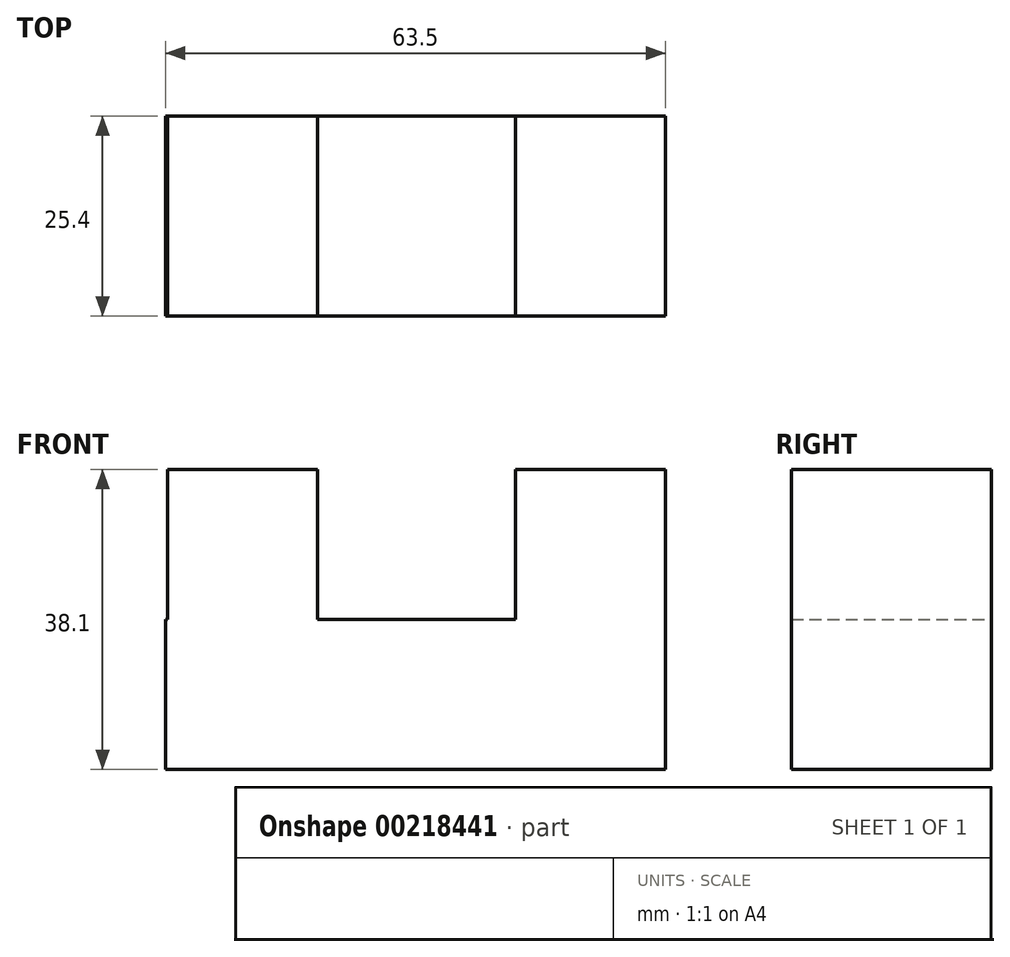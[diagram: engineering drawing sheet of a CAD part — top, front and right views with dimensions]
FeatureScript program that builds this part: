
annotation { "Feature Type Name" : "Feature", "Feature Type Description" : "" }
export const myFeature = defineFeature(function(context is Context, id is Id, definition is map)
    precondition{}
    {
        {
            var Q0;
            Q0=qCreatedBy(makeId("Front.planeOp"),FACE);
            var sketch = newSketch(context, id + "F0", { "sketchPlane" : qUnion([Q0])});
            skLineSegment(sketch, "E0.bottom", {"start": v(-17.5, 0) * mm, "end": v(-81, 0) * mm});
            skLineSegment(sketch, "E0.top", {"start": v(-17.5, 19.05) * mm, "end": v(-81, 19.05) * mm});
            skLineSegment(sketch, "E0.left", {"start": v(-17.5, 0) * mm, "end": v(-17.5, 19.05) * mm});
            skLineSegment(sketch, "E0.right", {"start": v(-81, 0) * mm, "end": v(-81, 19.05) * mm});
            skPoint(sketch, "E0.middle", {"position": v(-49.24, 9.52) * mm});
            skLineSegment(sketch, "E1.bottom", {"start": v(-17.5, 19.05) * mm, "end": v(-36.54, 19.05) * mm});
            skLineSegment(sketch, "E1.top", {"start": v(-17.5, 38.1) * mm, "end": v(-36.54, 38.1) * mm});
            skLineSegment(sketch, "E1.left", {"start": v(-17.5, 19.05) * mm, "end": v(-17.5, 38.1) * mm});
            skLineSegment(sketch, "E1.right", {"start": v(-36.54, 19.05) * mm, "end": v(-36.54, 38.1) * mm});
            skPoint(sketch, "E1.middle", {"position": v(-27.02, 28.57) * mm});
            skLineSegment(sketch, "E2.bottom", {"start": v(-61.68, 19.05) * mm, "end": v(-80.73, 19.05) * mm});
            skLineSegment(sketch, "E2.top", {"start": v(-61.68, 38.1) * mm, "end": v(-80.73, 38.1) * mm});
            skLineSegment(sketch, "E2.left", {"start": v(-61.68, 19.05) * mm, "end": v(-61.68, 38.1) * mm});
            skLineSegment(sketch, "E2.right", {"start": v(-80.73, 19.05) * mm, "end": v(-80.73, 38.1) * mm});
            skPoint(sketch, "E2.middle", {"position": v(-71.2, 28.57) * mm});
            skSolve(sketch);
        }
        {
            var Q0;
            Q0 = qSketchRegion(id + "F0", true);
            extrude(context, id + "F1", {"entities" : qUnion([Q0]), "endBound" : BoundingType.SYMMETRIC, "depth" : 25.4 * mm});
        }
    });
